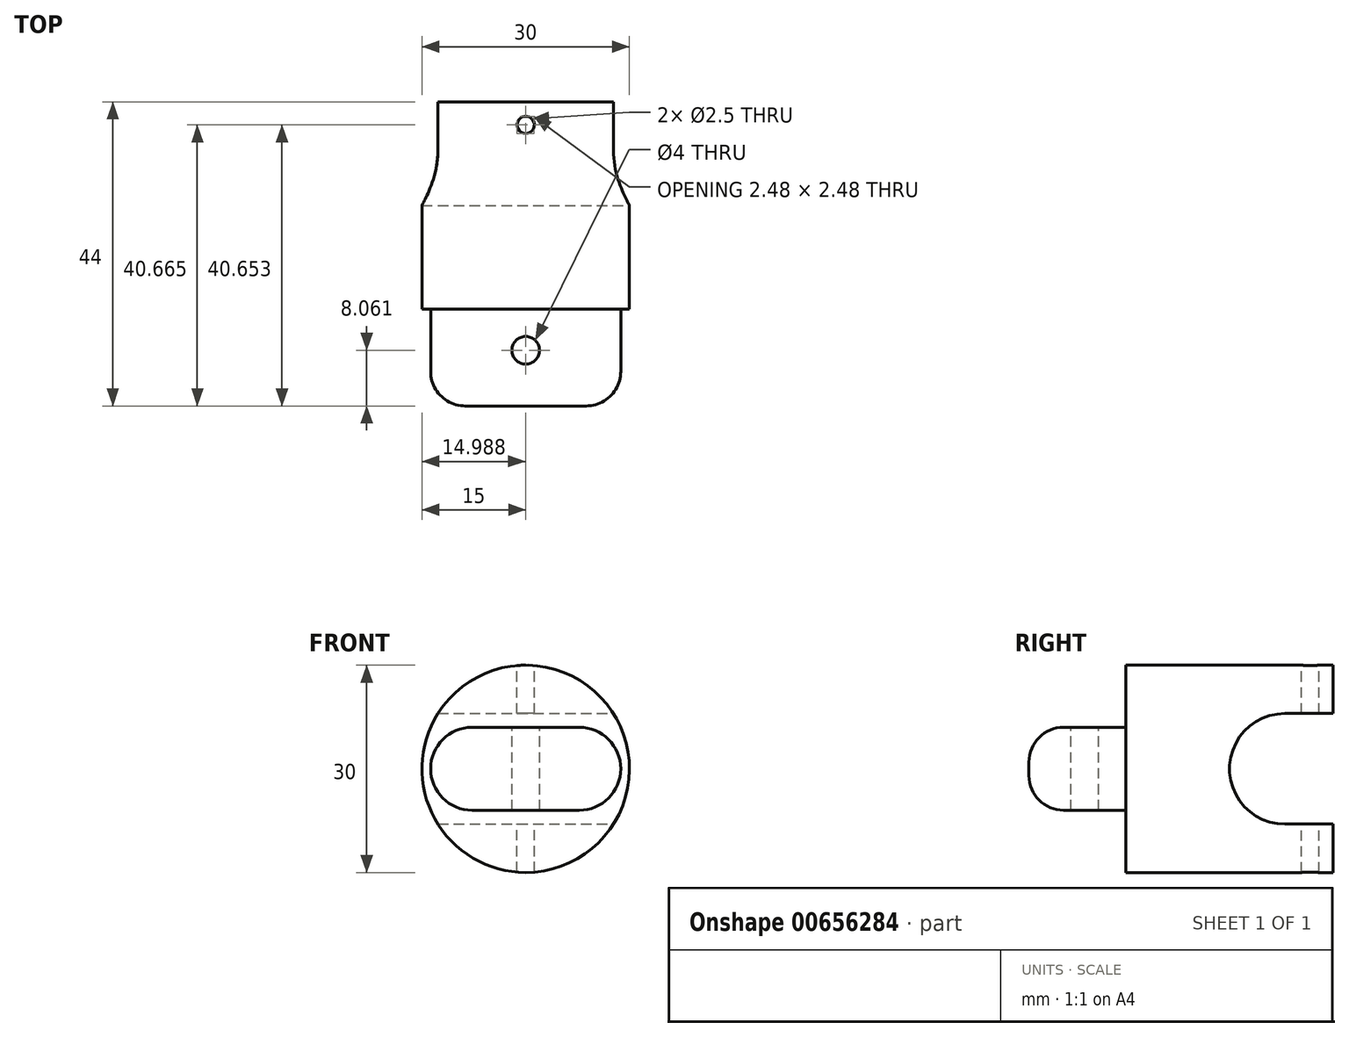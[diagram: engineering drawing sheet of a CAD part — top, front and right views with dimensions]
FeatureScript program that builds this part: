
annotation { "Feature Type Name" : "Feature", "Feature Type Description" : "" }
export const myFeature = defineFeature(function(context is Context, id is Id, definition is map)
    precondition{}
    {
        {
            var Q0;
            Q0=qCreatedBy(makeId("Front.planeOp"),FACE);
            var sketch = newSketch(context, id + "F0", { "sketchPlane" : qUnion([Q0])});
            skCircle(sketch, "E0", {"center": v(0, 0) * mm, "radius": 15 * mm});
            skSolve(sketch);
        }
        {
            var Q0;
            Q0 = qSketchRegion(id + "F0", true);
            extrude(context, id + "F1", {"entities" : qUnion([Q0]), "depth" : 30 * mm, "offsetDistance" : 25 * mm});
        }
        {
            var Q0;
            Q0=qCreatedBy(makeId("Right.planeOp"),FACE);
            var sketch = newSketch(context, id + "F2", { "sketchPlane" : qUnion([Q0])});
            skLineSegment(sketch, "E1.bottom", {"start": v(-7, 8) * mm, "end": v(15, 8) * mm});
            skLineSegment(sketch, "E1.top", {"start": v(-7, -8) * mm, "end": v(15, -8) * mm});
            skLineSegment(sketch, "E1.left", {"start": v(-15, 0) * mm, "end": v(-15, 0) * mm});
            skLineSegment(sketch, "E1.right", {"start": v(15, 8) * mm, "end": v(15, -8) * mm});
            skPoint(sketch, "E1.middle", {"position": v(0, 0) * mm});
            skPoint(sketch, "E2.visualSharp", {"position": v(-15, 8) * mm});
            skArc(sketch, "E2.filletArc", {"start": v(-7, 8) * mm, "mid": v(-12.66, 5.66) * mm, "end": v(-15, 0) * mm});
            skPoint(sketch, "E3.visualSharp", {"position": v(-15, -8) * mm});
            skArc(sketch, "E3.filletArc", {"start": v(-15, 0) * mm, "mid": v(-12.66, -5.66) * mm, "end": v(-7, -8) * mm});
            skSolve(sketch);
        }
        {
            var Q0;
            Q0 = qSketchRegion(id + "F2", true);
            extrude(context, id + "F3", {"entities" : qUnion([Q0]), "operationType" : NewBodyOperationType.REMOVE, "oppositeDirection" : true, "depth" : 25 * mm, "offsetDistance" : 25 * mm, "hasSecondDirection" : true, "secondDirectionOppositeDirection" : false, "secondDirectionDepth" : 25 * mm});
        }
        {
            var Q0;
            Q0=makeQuery(id+"F1.opExtrude","CAP_FACE",FACE,{"disambiguationData":[OSD([sQuery(id+"F0.wireOp",EDGE,"E0")])],"isStart":false});
            var sketch = newSketch(context, id + "F4", { "sketchPlane" : qUnion([Q0])});
            skLineSegment(sketch, "E4.bottom", {"start": v(7.75, 6) * mm, "end": v(-7.75, 6) * mm});
            skLineSegment(sketch, "E4.top", {"start": v(7.75, -6) * mm, "end": v(-7.75, -6) * mm});
            skLineSegment(sketch, "E4.left", {"start": v(13.75, 0) * mm, "end": v(13.75, 0) * mm});
            skLineSegment(sketch, "E4.right", {"start": v(-13.75, 0) * mm, "end": v(-13.75, 0) * mm});
            skPoint(sketch, "E4.middle", {"position": v(0, 0) * mm});
            skPoint(sketch, "E5.visualSharp", {"position": v(-13.75, 6) * mm});
            skArc(sketch, "E5.filletArc", {"start": v(-7.75, 6) * mm, "mid": v(-12, 4.24) * mm, "end": v(-13.75, 0) * mm});
            skPoint(sketch, "E6.visualSharp", {"position": v(-13.75, -6) * mm});
            skArc(sketch, "E6.filletArc", {"start": v(-13.75, 0) * mm, "mid": v(-12, -4.24) * mm, "end": v(-7.75, -6) * mm});
            skPoint(sketch, "E7.visualSharp", {"position": v(13.75, -6) * mm});
            skArc(sketch, "E7.filletArc", {"start": v(7.75, -6) * mm, "mid": v(12, -4.24) * mm, "end": v(13.75, 0) * mm});
            skPoint(sketch, "E8.visualSharp", {"position": v(13.75, 6) * mm});
            skArc(sketch, "E8.filletArc", {"start": v(13.75, 0) * mm, "mid": v(12, 4.24) * mm, "end": v(7.75, 6) * mm});
            skSolve(sketch);
        }
        {
            var Q0;
            Q0 = qSketchRegion(id + "F4", true);
            extrude(context, id + "F5", {"entities" : qUnion([Q0]), "operationType" : NewBodyOperationType.ADD, "depth" : 14 * mm, "offsetDistance" : 25 * mm});
        }
        {
            var Q0;
            Q0=makeQuery(id+"F5.opExtrude","CAP_EDGE",EDGE,{"disambiguationData":[OSD([sQuery(id+"F4.wireOp",EDGE,"E7.filletArc"),sQuery(id+"F4.wireOp",EDGE,"E8.filletArc")])],"isStart":false});
            fillet(context, id + "F6", {"entities" : qUnion([Q0]), "radius" : 5 * mm, "tangentPropagation" : true, "allowEdgeOverflow" : false});
        }
        {
            var Q0;
            Q0=qCreatedBy(makeId("Top.planeOp"),FACE);
            var sketch = newSketch(context, id + "F7", { "sketchPlane" : qUnion([Q0])});
            skCircle(sketch, "E9", {"center": v(0, -35.94) * mm, "radius": 2 * mm});
            skSolve(sketch);
        }
        {
            var Q0;
            Q0 = qSketchRegion(id + "F7", true);
            extrude(context, id + "F8", {"entities" : qUnion([Q0]), "operationType" : NewBodyOperationType.REMOVE, "oppositeDirection" : true, "depth" : 25 * mm, "offsetDistance" : 25 * mm, "hasSecondDirection" : true, "secondDirectionOppositeDirection" : false, "secondDirectionDepth" : 25 * mm});
        }
        {
            var Q0;
            Q0=qCreatedBy(makeId("Top.planeOp"),FACE);
            var sketch = newSketch(context, id + "F9", { "sketchPlane" : qUnion([Q0])});
            skCircle(sketch, "E10", {"center": v(0, -3.33) * mm, "radius": 1.25 * mm});
            skSolve(sketch);
        }
        {
            var Q0;
            Q0 = qSketchRegion(id + "F9", true);
            extrude(context, id + "F10", {"entities" : qUnion([Q0]), "operationType" : NewBodyOperationType.REMOVE, "oppositeDirection" : true, "depth" : 25 * mm, "offsetDistance" : 25 * mm, "hasSecondDirection" : true, "secondDirectionOppositeDirection" : false, "secondDirectionDepth" : 25 * mm});
        }
    });
